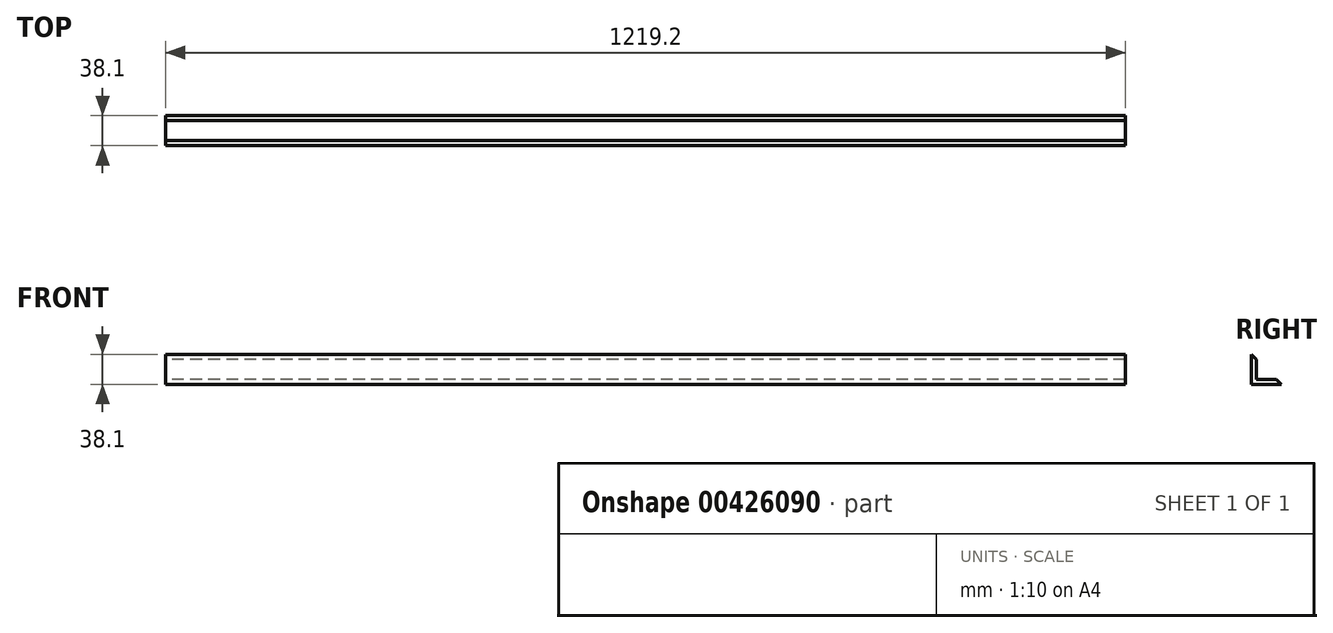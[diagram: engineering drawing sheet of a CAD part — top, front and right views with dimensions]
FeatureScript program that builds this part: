
annotation { "Feature Type Name" : "Feature", "Feature Type Description" : "" }
export const myFeature = defineFeature(function(context is Context, id is Id, definition is map)
    precondition{}
    {
        {
            var Q0;
            Q0=qCreatedBy(makeId("Right.planeOp"),FACE);
            var sketch = newSketch(context, id + "F0", { "sketchPlane" : qUnion([Q0])});
            skLineSegment(sketch, "E0", {"start": v(0, 38.1) * mm, "end": v(0, 0) * mm});
            skLineSegment(sketch, "E1", {"start": v(0, 0) * mm, "end": v(38.1, 0) * mm});
            skLineSegment(sketch, "E2", {"start": v(38.1, 0) * mm, "end": v(31.75, 6.35) * mm});
            skLineSegment(sketch, "E3", {"start": v(31.75, 6.35) * mm, "end": v(6.35, 6.35) * mm});
            skLineSegment(sketch, "E4", {"start": v(6.35, 6.35) * mm, "end": v(6.35, 31.75) * mm});
            skLineSegment(sketch, "E5", {"start": v(6.35, 31.75) * mm, "end": v(0, 38.1) * mm});
            skSolve(sketch);
        }
        {
            var Q0;
            Q0=makeQuery(id+"F0.imprint","IMPRINT",FACE,{"disambiguationData":[TD([[makeQuery(id+"F0.imprint","IMPRINT",EDGE,{"derivedFrom":sQuery(id+"F0.wireOp",EDGE,"E0")}),1.0]])]});
            extrude(context, id + "F1", {"entities" : qUnion([Q0]), "depth" : 1219.2 * mm});
        }
    });
